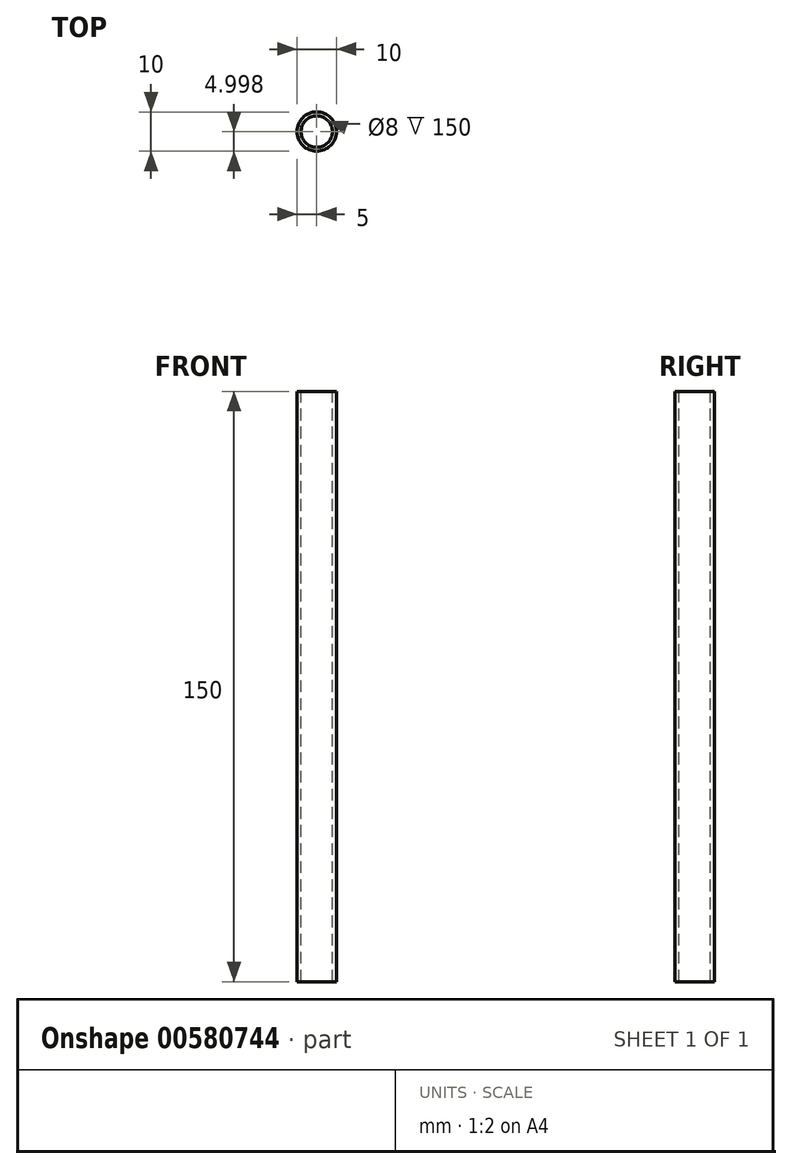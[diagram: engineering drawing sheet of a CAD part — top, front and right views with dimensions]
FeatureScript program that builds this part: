
annotation { "Feature Type Name" : "Feature", "Feature Type Description" : "" }
export const myFeature = defineFeature(function(context is Context, id is Id, definition is map)
    precondition{}
    {
        {
            var Q0;
            Q0=qCreatedBy(makeId("Top.planeOp"),FACE);
            var sketch = newSketch(context, id + "F0", { "sketchPlane" : qUnion([Q0])});
            skCircle(sketch, "E0", {"center": v(0, -1.5) * mm, "radius": 5 * mm});
            skSolve(sketch);
        }
        {
            var Q0;
            Q0=makeQuery(id+"F0.imprint","IMPRINT",FACE,{"disambiguationData":[TD([[makeQuery(id+"F0.imprint","IMPRINT",EDGE,{"derivedFrom":sQuery(id+"F0.wireOp",EDGE,"E0")}),1.0]])]});
            extrude(context, id + "F1", {"entities" : qUnion([Q0]), "depth" : 150 * mm, "offsetDistance" : 25.4 * mm});
        }
        {
            var Q0;
            Q0=makeQuery(id+"F1.opExtrude","CAP_FACE",FACE,{"disambiguationData":[OSD([sQuery(id+"F0.wireOp",EDGE,"E0")])],"isStart":false});
            var sketch = newSketch(context, id + "F2", { "sketchPlane" : qUnion([Q0])});
            skPoint(sketch, "E1", {"position": v(0, -1.5) * mm});
            skSolve(sketch);
        }
        {
            var Q0;
            Q0=sQuery(id+"F2.wireOp",VERTEX,"E1");
            var Q1;
            Q1=makeQuery(id+"F1.opExtrude","SWEPT_BODY",BODY,{"disambiguationData":[OSD([sQuery(id+"F0.wireOp",EDGE,"E0")])]});
            hole(context, id + "F3", {"style" : HoleStyle.SIMPLE, "endStyle" : HoleEndStyle.THROUGH, "holeDiameter" : 8 * mm, "isTappedThrough" : true, "tappedDepth" : 12 * mm, "tapClearance" : 3, "locations" : qUnion([Q0]), "scope" : qUnion([Q1])});
        }
    });
